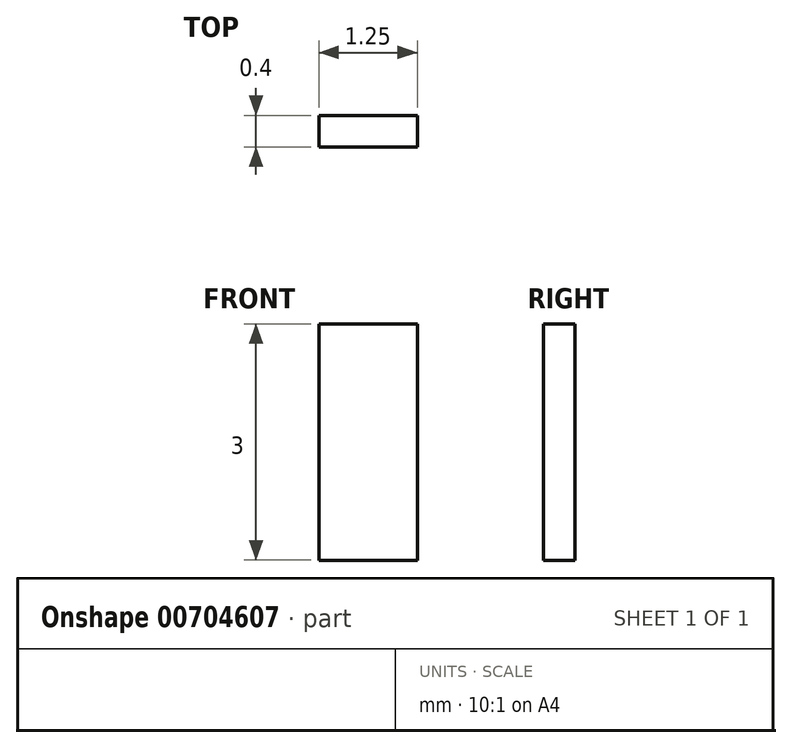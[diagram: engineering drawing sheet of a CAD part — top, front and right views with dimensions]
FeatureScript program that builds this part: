
annotation { "Feature Type Name" : "Feature", "Feature Type Description" : "" }
export const myFeature = defineFeature(function(context is Context, id is Id, definition is map)
    precondition{}
    {
        {
            var Q0;
            Q0=qCreatedBy(makeId("Front.planeOp"),FACE);
            var sketch = newSketch(context, id + "F0", { "sketchPlane" : qUnion([Q0])});
            skLineSegment(sketch, "E0", {"start": v(-23.29, 12.9) * mm, "end": v(-22.04, 12.9) * mm});
            skLineSegment(sketch, "E1", {"start": v(-22.04, 12.9) * mm, "end": v(-22.04, 9.9) * mm});
            skLineSegment(sketch, "E2", {"start": v(-22.04, 9.9) * mm, "end": v(-23.29, 9.9) * mm});
            skLineSegment(sketch, "E3", {"start": v(-23.29, 9.9) * mm, "end": v(-23.29, 12.9) * mm});
            skSolve(sketch);
        }
        {
            var Q0;
            Q0 = qSketchRegion(id + "F0", true);
            extrude(context, id + "F1", {"entities" : qUnion([Q0]), "depth" : 0.4 * mm, "offsetDistance" : 25 * mm});
        }
    });
